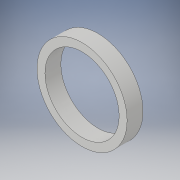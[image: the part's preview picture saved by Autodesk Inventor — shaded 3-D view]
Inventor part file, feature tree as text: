
AUTODESK INVENTOR PART (.ipt)
format: ipt  version: 2019 (Build 230136000, 136)  size: 101,888 bytes
history: native  units: mm
features: extrude x1, sketch x1
ambient origin geometry x8: Origin, YZ Plane, XZ Plane, XY Plane, X Axis, Y Axis, Z Axis, Center Point
bodies: Solid1 (feature_tree)
feature tree (2):
  extrude  "Extrusion1"  Depth=30.0mm
  sketch  "Sketch1"  dims[d0=140.0mm d1=170.0mm d2=30.0mm d3=0.0mm]
